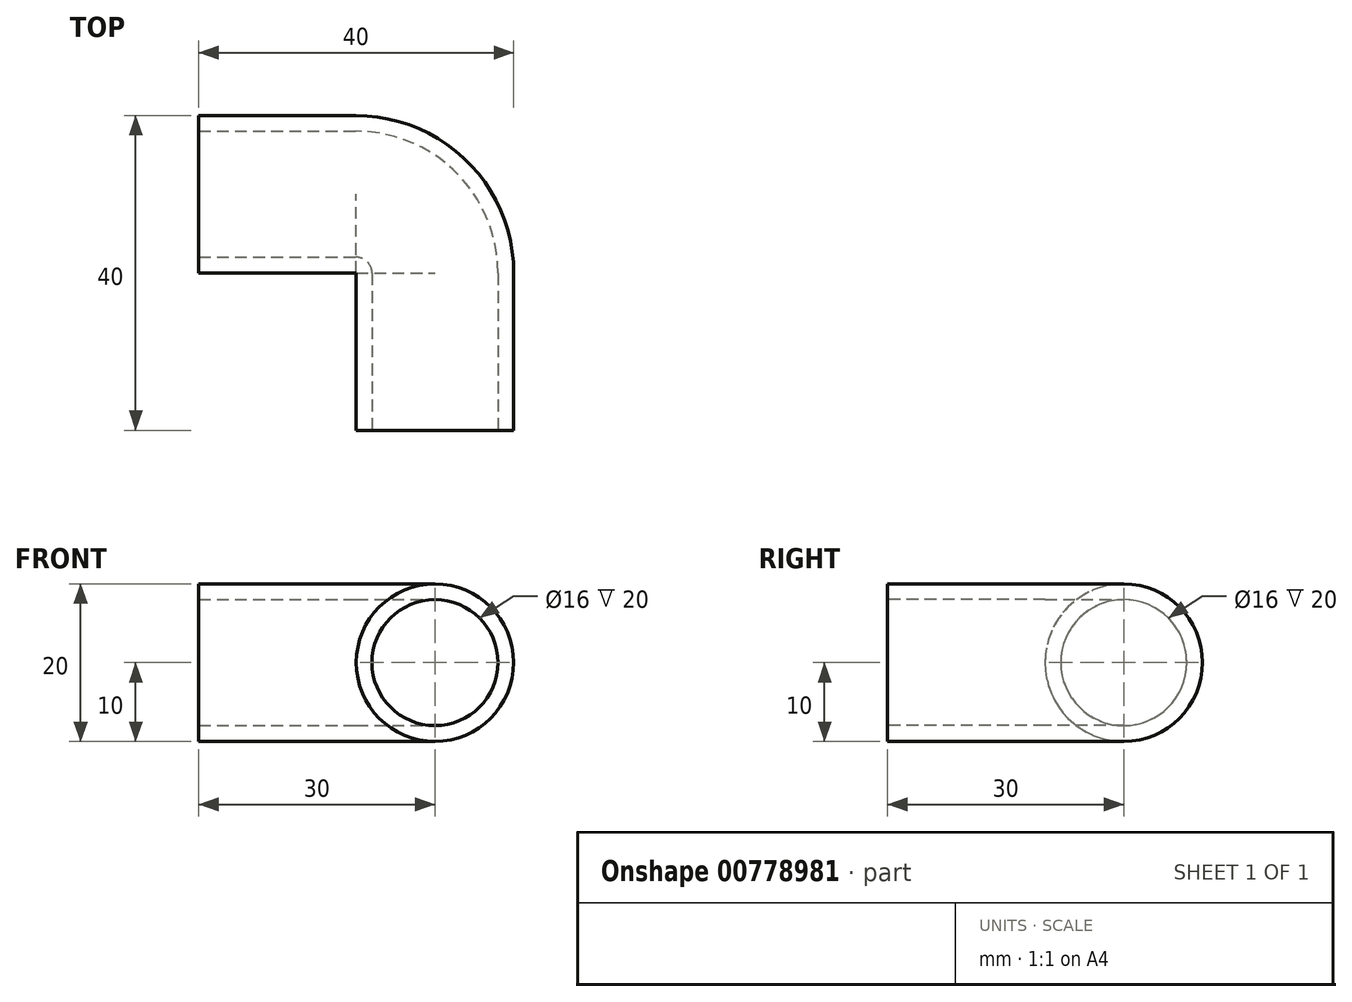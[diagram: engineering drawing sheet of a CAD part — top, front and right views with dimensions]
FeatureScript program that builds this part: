
annotation { "Feature Type Name" : "Feature", "Feature Type Description" : "" }
export const myFeature = defineFeature(function(context is Context, id is Id, definition is map)
    precondition{}
    {
        {
            var Q0;
            Q0=qCreatedBy(makeId("Top.planeOp"),FACE);
            var sketch = newSketch(context, id + "F0", { "sketchPlane" : qUnion([Q0])});
            skLineSegment(sketch, "E0", {"start": v(-10, 0) * mm, "end": v(-30, 0) * mm});
            skLineSegment(sketch, "E1", {"start": v(0, -10) * mm, "end": v(0, -30) * mm});
            skPoint(sketch, "E2.visualSharp", {"position": v(0, 0) * mm});
            skArc(sketch, "E2.filletArc", {"start": v(0, -10) * mm, "mid": v(-2.93, -2.93) * mm, "end": v(-10, 0) * mm});
            skSolve(sketch);
        }
        {
            var Q0;
            Q0=qCreatedBy(makeId("Right.planeOp"),FACE);
            cPlane(context, id + "F1", {"entities" : qUnion([Q0]), "cplaneType" : CPlaneType.OFFSET, "offset" : 25 * mm, "oppositeDirection" : true, "width" : 150 * mm, "height" : 150 * mm});
        }
        {
            var Q0;
            Q0=qCreatedBy(id+"F1.planeOp",FACE);
            var sketch = newSketch(context, id + "F2", { "sketchPlane" : qUnion([Q0])});
            skCircle(sketch, "E3", {"center": v(0, 0) * mm, "radius": 10 * mm});
            skCircle(sketch, "E4.0", {"center": v(0, 0) * mm, "radius": 8 * mm});
            skSolve(sketch);
        }
        {
            var Q0;
            Q0 = qSketchRegion(id + "F2", true);
            var Q1;
            Q1 = qConstructionFilter(qBodyType(qCreatedBy(id + "F0" ,EDGE), BodyType.WIRE), ConstructionObject.NO);
            sweep(context, id + "F3", {"profiles" : qUnion([Q0]), "path" : qUnion([Q1])});
        }
    });
